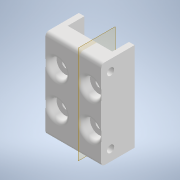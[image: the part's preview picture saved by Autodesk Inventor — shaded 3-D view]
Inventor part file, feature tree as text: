
AUTODESK INVENTOR PART (.ipt)
format: ipt  version: 2022 (Build 260153000, 153)  size: 228,352 bytes
history: native  units: in
note: dims shown in document units (in); Inventor stores cm internally (conversion verified against a paired STEP export)
features: reference x12, sketch x8, other x8, extrude x7, fillet x4, plane x2
ambient origin geometry x8: Origin, YZ Plane, XZ Plane, XY Plane, X Axis, Y Axis, Z Axis, Center Point
bodies: Solid1 (feature_tree)
feature tree (41):
  extrude  "Extrusion1"  Depth=1.3381in TaperAngle=0.0deg
  extrude  "Extrusion2"  Depth=0.315in
  extrude  "Extrusion4"  Depth=0.315in
  extrude  "Extrusion5"  Depth=0.1575in
  plane  "Work Plane1"
  extrude  "Extrusion6"  Depth=0.0984in
  extrude  "Extrusion7"  [1 undecoded]
  plane  "Work Plane2"
  sketch  "Sketch8"  dims[d24=1.0in d25=0.1575in d26=0.25in d27=0.0in d28=0.375in d29=0.0in d30=1.0157in d31=-0.0394in]
  extrude  "Extrusion8"  Depth=0.1575in
  fillet  "Fillet1"  Radius=0.25in
  fillet  "Fillet2"  Radius=0.375in
  fillet  "Fillet3"  Radius=1.0157in
  fillet  "Fillet4"  [1 undecoded]
  sketch  "Sketch1"  dims[d1=0.2953in d2=0.0in d3=1.3381in d4=0.0in]
  reference  "Reference1"
  reference  "Reference2"
  reference  "Reference3"
  reference  "Reference4"
  sketch  "Sketch2"  dims[d10=0.315in d11=0.315in]
  reference  "Reference5"
  reference  "Reference6"
  reference  "Reference7"
  reference  "Reference8"
  reference  "Reference9"
  reference  "Reference10"
  sketch  "Sketch4"  dims[d12=0.315in d13=0.315in]
  sketch  "Sketch5"  dims[d14=0.1575in d15=0.0in d18=0.7874in]
  sketch  "Sketch6"  dims[d19=0.9843in d20=0.0984in]
  reference  "Reference15"
  reference  "Reference16"
  sketch  "Sketch7"  dims[d21=0.2953in d22=0.0in d23=-0.375in]
  sketch  "Sketch9"  dims[d32=0.9375in d33=0.0in d34=0.25in d35=0.125in d36=0.25in d37=0.0625in]
  parser-record x1  (decoder bookkeeping rows leaked as tree rows — omitted from the tree; the rows remain in map.json)
  other  "speedyPrinty.iam"
  other  "MGN9-H-block v1:1"
  other  "ToolChanger:1"
  other  "toolhead v2.iam"
  other  "volcano tool:1"
  other  "sherpa_mini_release1:1"
  other  "back plate:1"
note: 2 required parameter values undecoded (feature->parameter linkage not recoverable at this tier; creation-order binding heuristic only, values carry confidence <= 0.55)
note: 1 file-system path scrubbed to <path> (originals preserved in map.json)
